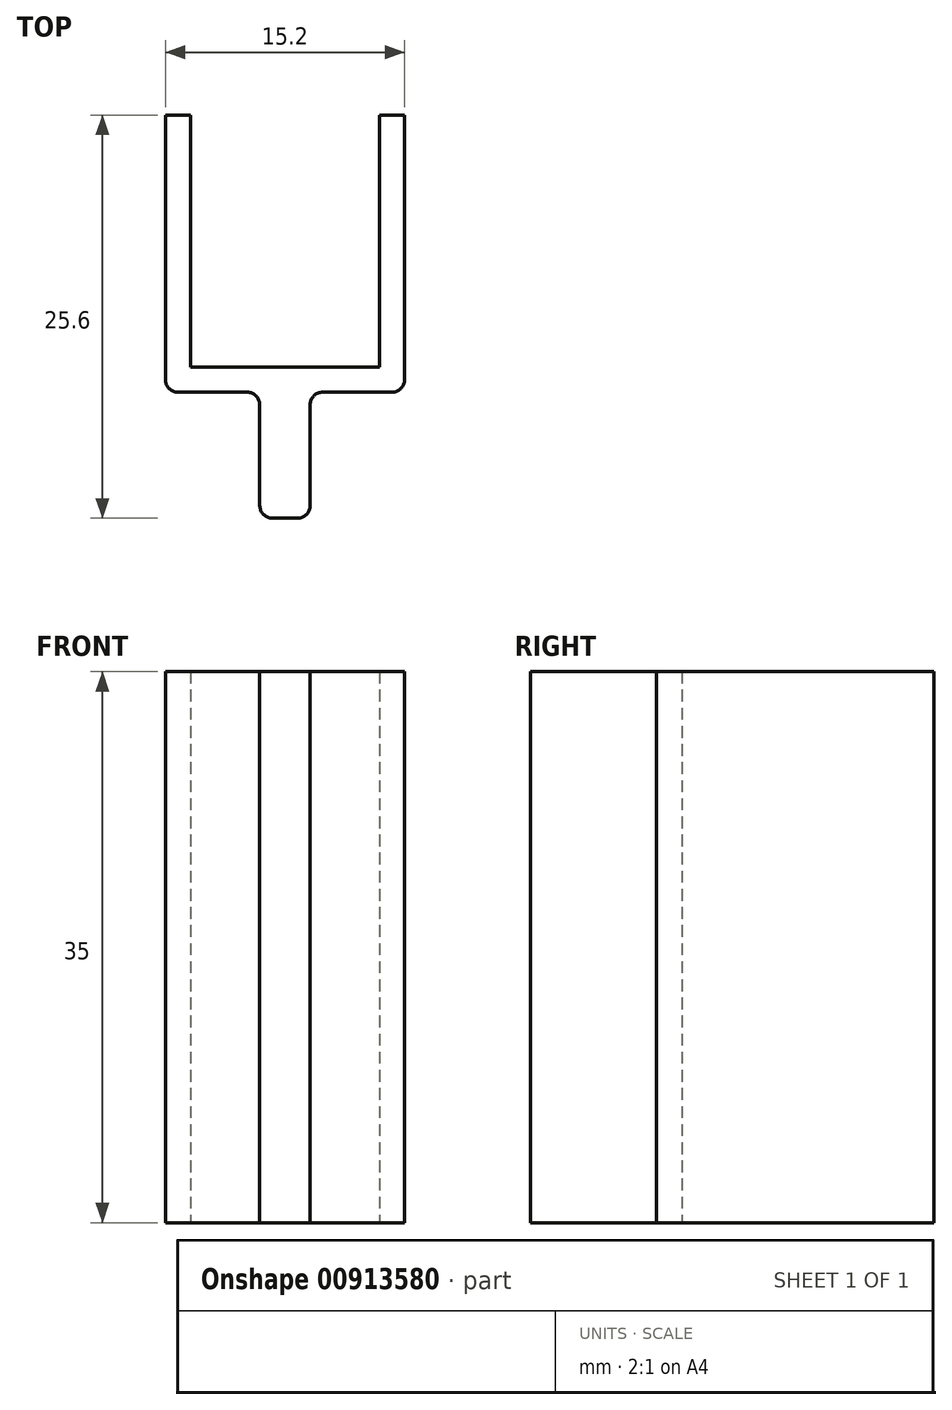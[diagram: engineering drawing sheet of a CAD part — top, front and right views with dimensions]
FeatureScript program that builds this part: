
annotation { "Feature Type Name" : "Feature", "Feature Type Description" : "" }
export const myFeature = defineFeature(function(context is Context, id is Id, definition is map)
    precondition{}
    {
        {
            var Q0;
            Q0=qCreatedBy(makeId("Top.planeOp"),FACE);
            var sketch = newSketch(context, id + "F0", { "sketchPlane" : qUnion([Q0])});
            skLineSegment(sketch, "E0.bottom", {"start": v(0, 0) * mm, "end": v(-12, 0) * mm});
            skLineSegment(sketch, "E0.left", {"start": v(0, 0) * mm, "end": v(0, 16) * mm});
            skLineSegment(sketch, "E0.right", {"start": v(-12, 0) * mm, "end": v(-12, 16) * mm});
            skLineSegment(sketch, "E1.bottom", {"start": v(1.6, -1.6) * mm, "end": v(-13.6, -1.6) * mm});
            skLineSegment(sketch, "E1.left", {"start": v(1.6, -1.6) * mm, "end": v(1.6, 16) * mm});
            skLineSegment(sketch, "E1.right", {"start": v(-13.6, -1.6) * mm, "end": v(-13.6, 16) * mm});
            skLineSegment(sketch, "E2", {"start": v(-12, 16) * mm, "end": v(-13.6, 16) * mm});
            skLineSegment(sketch, "E3", {"start": v(-13.6, 16) * mm, "end": v(-12, 16) * mm});
            skLineSegment(sketch, "E4", {"start": v(0, 16) * mm, "end": v(1.6, 16) * mm});
            skLineSegment(sketch, "E5", {"start": v(-6, -4.52) * mm, "end": v(-6, 27.93) * mm, "construction": true});
            skPoint(sketch, "E5.startSnap0", {"position": v(-6, -1.6) * mm});
            skLineSegment(sketch, "E6.MirrorCS", {"start": v(1.6, 16) * mm, "end": v(0, 16) * mm});
            skPoint(sketch, "E7.MirrorCS.start.orphan", {"position": v(0, 16) * mm});
            skPoint(sketch, "E8.MirrorCS.start.orphan", {"position": v(1.6, 16) * mm});
            skLineSegment(sketch, "E9", {"start": v(-7.6, -1.6) * mm, "end": v(-7.6, -9.6) * mm});
            skLineSegment(sketch, "E10", {"start": v(-7.6, -9.6) * mm, "end": v(-4.4, -9.6) * mm});
            skLineSegment(sketch, "E11", {"start": v(-4.4, -9.6) * mm, "end": v(-4.4, -1.6) * mm});
            skPoint(sketch, "E12", {"position": v(-6, -9.6) * mm});
            skSolve(sketch);
        }
        {
            var Q0;
            Q0=qSketchRegion(id+"F0",true);
            extrude(context, id + "F1", {"entities" : qUnion([Q0]), "depth" : 35 * mm, "offsetDistance" : 25 * mm});
        }
        {
            var Q0;
            Q0=makeQuery(id+"F1.opExtrude","SWEPT_EDGE",EDGE,{"disambiguationData":[OSD([sQuery(id+"F0.wireOp",EDGE,"E1.bottom"),sQuery(id+"F0.wireOp",EDGE,"E1.left")])]});
            var Q1;
            Q1=makeQuery(id+"F1.opExtrude","SWEPT_EDGE",EDGE,{"disambiguationData":[OSD([sQuery(id+"F0.wireOp",EDGE,"E1.bottom"),sQuery(id+"F0.wireOp",EDGE,"E1.right")])]});
            var Q2;
            Q2=makeQuery(id+"F1.opExtrude","SWEPT_EDGE",EDGE,{"disambiguationData":[OSD([sQuery(id+"F0.wireOp",EDGE,"58cdd0fb-2654-4180-8f26-8b1f058e392d.top"),sQuery(id+"F0.wireOp",EDGE,"58cdd0fb-2654-4180-8f26-8b1f058e392d.left")])]});
            var Q3;
            Q3=makeQuery(id+"F1.opExtrude","SWEPT_EDGE",EDGE,{"disambiguationData":[OSD([sQuery(id+"F0.wireOp",EDGE,"799665ce-0ac7-41e6-8499-f53fd8c64e8c5.MirrorCS"),sQuery(id+"F0.wireOp",EDGE,"799665ce-0ac7-41e6-8499-f53fd8c64e8c6.MirrorCS")])]});
            var Q4;
            Q4=makeQuery(id+"F1.opExtrude","SWEPT_EDGE",EDGE,{"disambiguationData":[OSD([sQuery(id+"F0.wireOp",EDGE,"799665ce-0ac7-41e6-8499-f53fd8c64e8c5.MirrorCS"),sQuery(id+"F0.wireOp",EDGE,"799665ce-0ac7-41e6-8499-f53fd8c64e8c8.MirrorCS")])]});
            var Q5;
            Q5=makeQuery(id+"F1.opExtrude","SWEPT_EDGE",EDGE,{"disambiguationData":[OSD([sQuery(id+"F0.wireOp",EDGE,"58cdd0fb-2654-4180-8f26-8b1f058e392d.top"),sQuery(id+"F0.wireOp",EDGE,"58cdd0fb-2654-4180-8f26-8b1f058e392d.right")])]});
            var Q6;
            Q6=makeQuery(id+"F1.opExtrude","SWEPT_EDGE",EDGE,{"disambiguationData":[OSD([sQuery(id+"F0.wireOp",EDGE,"E1.bottom"),sQuery(id+"F0.wireOp",EDGE,"E9")])]});
            var Q7;
            Q7=makeQuery(id+"F1.opExtrude","SWEPT_EDGE",EDGE,{"disambiguationData":[OSD([sQuery(id+"F0.wireOp",EDGE,"E1.bottom"),sQuery(id+"F0.wireOp",EDGE,"E11")])]});
            var Q8;
            Q8=makeQuery(id+"F1.opExtrude","SWEPT_EDGE",EDGE,{"disambiguationData":[OSD([sQuery(id+"F0.wireOp",EDGE,"E9"),sQuery(id+"F0.wireOp",EDGE,"E10")])]});
            var Q9;
            Q9=makeQuery(id+"F1.opExtrude","SWEPT_EDGE",EDGE,{"disambiguationData":[OSD([sQuery(id+"F0.wireOp",EDGE,"E10"),sQuery(id+"F0.wireOp",EDGE,"E11")])]});
            fillet(context, id + "F2", {"entities" : qUnion([Q0, Q1, Q2, Q3, Q4, Q5, Q6, Q7, Q8, Q9]), "radius" : .8 * mm, "tangentPropagation" : true, "allowEdgeOverflow" : false});
        }
    });
